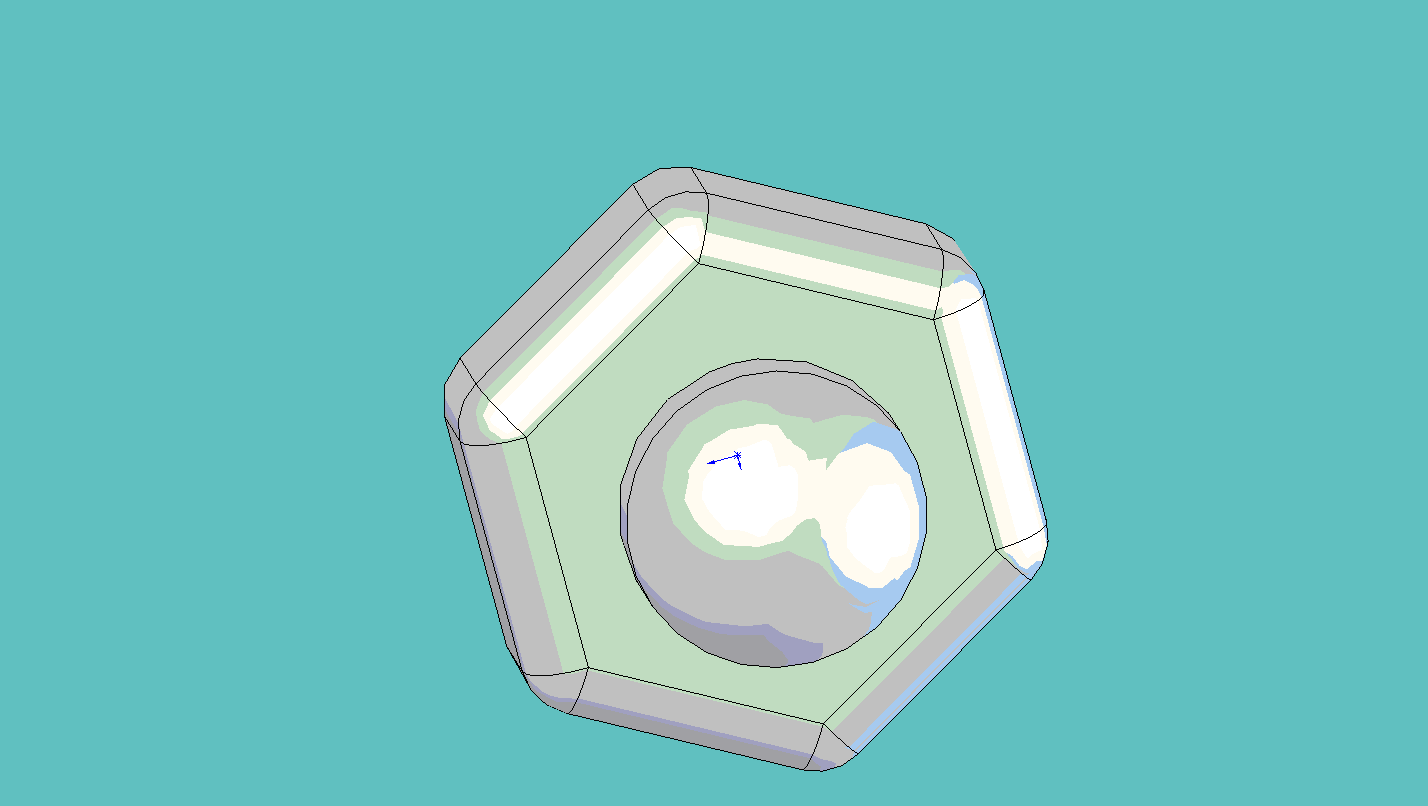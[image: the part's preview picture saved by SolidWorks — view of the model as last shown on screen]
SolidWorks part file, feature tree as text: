
SOLIDWORKS PART (.sldprt)
format: sldprt  version: not decoded by parser v0  size: 159,232 bytes
history: native  units: mm
features: sketch x4, extrude x4, material x1, chamfer x1, dome x1, fillet x1 (+13 scaffold rows collapsed)
feature tree (25):
  scaffold x13  (default folders/planes/origin — collapsed)
  material  "Material <not specified>"
  sketch  "Sketch1"  dims[D1=6.096mm]
  extrude  "Extrude1"  Depth=8.89mm
  chamfer  "Chamfer1"  Distance=1.27mm Angle=45deg
  sketch  "Sketch2"  dims[D1=11.43mm]
  extrude  "Extrude2"  Depth=3.81mm
  sketch  "Sketch3"
  extrude  "Extrude3"  Depth=1.27mm
  sketch  "Sketch4"  dims[D1=6.35mm]
  extrude  "Extrude4"  Depth=1.27mm
  dome  "Dome1"
  fillet  "Fillet1"  Radius=1.27mm
decode coverage: 9 of 11 modeling features carry decoded parameters
note: suppression state not decoded; provenance and decode notes live in map.json
